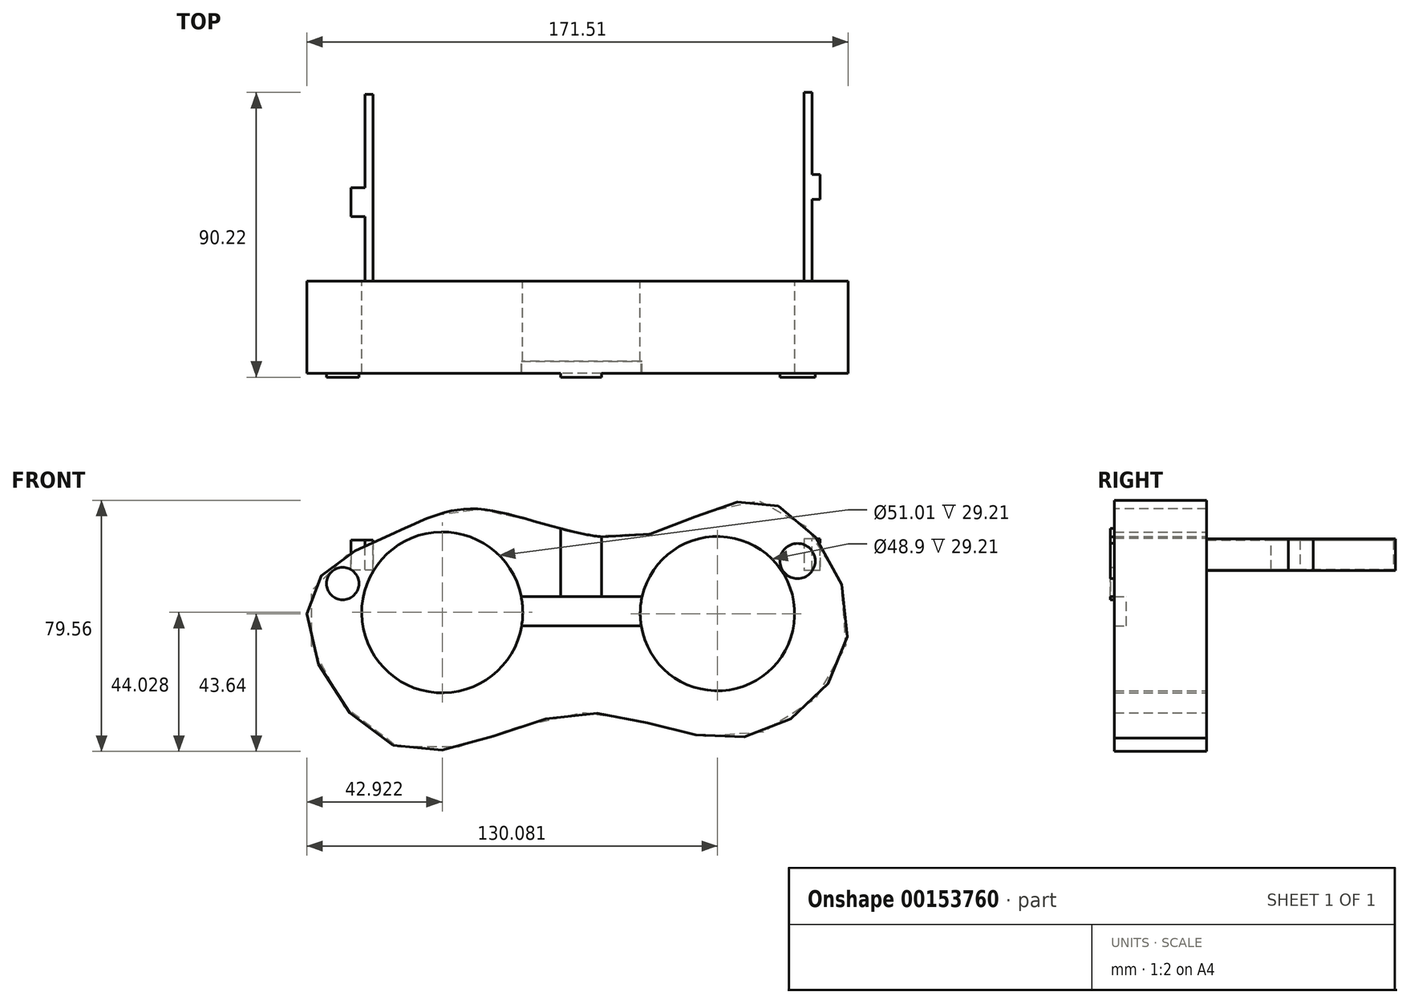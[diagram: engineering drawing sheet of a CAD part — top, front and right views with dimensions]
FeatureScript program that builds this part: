
annotation { "Feature Type Name" : "Feature", "Feature Type Description" : "" }
export const myFeature = defineFeature(function(context is Context, id is Id, definition is map)
    precondition{}
    {
        {
            var Q0;
            Q0=qCreatedBy(makeId("Front.planeOp"),FACE);
            var sketch = newSketch(context, id + "F0", { "sketchPlane" : qUnion([Q0])});
            skCircle(sketch, "E0", {"center": v(-40.35, 13.8) * mm, "radius": 25.5 * mm});
            skCircle(sketch, "E1", {"center": v(46.81, 13.42) * mm, "radius": 24.45 * mm});
            skLineSegment(sketch, "E2", {"start": v(-15.34, 18.84) * mm, "end": v(22.97, 18.84) * mm});
            skLineSegment(sketch, "E3", {"start": v(22.97, 18.84) * mm, "end": v(22.66, 9.61) * mm});
            skLineSegment(sketch, "E4", {"start": v(22.66, 9.61) * mm, "end": v(-15.19, 9.61) * mm});
            skLineSegment(sketch, "E5", {"start": v(-15.19, 9.61) * mm, "end": v(-15.34, 18.84) * mm});
            skFitSpline(sketch, "E6", {"points": [v(-55.43, 39.07) * mm, v(-28.2, 46.52) * mm, v(20.76, 37.7) * mm, v(62.09, 48.87) * mm, v(88.14, 7.74) * mm, v(54.25, -25.76) * mm, v(2.15, -18.12) * mm, v(-54.25, -28.89) * mm, v(-82.85, 17.14) * mm, v(-55.43, 39.07) * mm]});
            skSolve(sketch);
        }
        {
            var Q0;
            Q0 = qSketchRegion(id + "F0", true);
            extrude(context, id + "F1", {"entities" : qUnion([Q0]), "depth" : 29.2 * mm});
        }
        {
            var Q0;
            Q0=qCreatedBy(makeId("Right.planeOp"),FACE);
            var sketch = newSketch(context, id + "F2", { "sketchPlane" : qUnion([Q0])});
            skLineSegment(sketch, "E7", {"start": v(0, 37.12) * mm, "end": v(59.74, 37.12) * mm});
            skLineSegment(sketch, "E8", {"start": v(59.74, 37.12) * mm, "end": v(59.74, 27.13) * mm});
            skLineSegment(sketch, "E9", {"start": v(59.74, 27.13) * mm, "end": v(0, 27.13) * mm});
            skLineSegment(sketch, "E10", {"start": v(0, 37.12) * mm, "end": v(0, 27.13) * mm});
            skSolve(sketch);
        }
        {
            var Q0;
            Q0 = qSketchRegion(id + "F2", true);
            extrude(context, id + "F3", {"entities" : qUnion([Q0]), "depth" : 2.54 * mm});
        }
        {
            var Q0;
            Q0=makeQuery(id+"F3.opExtrude","SWEPT_BODY",BODY,{"disambiguationData":[OSD([sQuery(id+"F2.wireOp",EDGE,"E7"),sQuery(id+"F2.wireOp",EDGE,"E8"),sQuery(id+"F2.wireOp",EDGE,"E9"),sQuery(id+"F2.wireOp",EDGE,"E10")])]});
            var Q1;
            Q1=qCreatedBy(makeId("Right.planeOp"),FACE);
            transform(context, id + "F4", {"entities" : qUnion([Q0]), "transformType" : TransformType.TRANSLATION_DISTANCE, "transformDirection" : qUnion([Q1]), "distance" : 74.3 * mm, "makeCopy" : false});
        }
        {
            var Q0;
            Q0=qCreatedBy(makeId("Right.planeOp"),FACE);
            var sketch = newSketch(context, id + "F5", { "sketchPlane" : qUnion([Q0])});
            skLineSegment(sketch, "E11", {"start": v(0, 36.72) * mm, "end": v(59.15, 36.72) * mm});
            skLineSegment(sketch, "E12", {"start": v(59.15, 36.72) * mm, "end": v(59.15, 27.32) * mm});
            skLineSegment(sketch, "E13", {"start": v(59.15, 27.32) * mm, "end": v(0, 27.32) * mm});
            skLineSegment(sketch, "E14", {"start": v(0, 27.32) * mm, "end": v(0, 36.72) * mm});
            skSolve(sketch);
        }
        {
            var Q0;
            Q0 = qSketchRegion(id + "F5", true);
            extrude(context, id + "F6", {"entities" : qUnion([Q0]), "oppositeDirection" : true, "depth" : 2.54 * mm});
        }
        {
            var Q0;
            Q0=makeQuery(id+"F6.opExtrude","SWEPT_BODY",BODY,{"disambiguationData":[OSD([sQuery(id+"F5.wireOp",EDGE,"E11"),sQuery(id+"F5.wireOp",EDGE,"E12"),sQuery(id+"F5.wireOp",EDGE,"E13"),sQuery(id+"F5.wireOp",EDGE,"E14")])]});
            var Q1;
            Q1=makeQuery(id+"F6.opExtrude","CAP_FACE",FACE,{"disambiguationData":[OSD([sQuery(id+"F5.wireOp",EDGE,"E11"),sQuery(id+"F5.wireOp",EDGE,"E12"),sQuery(id+"F5.wireOp",EDGE,"E13"),sQuery(id+"F5.wireOp",EDGE,"E14")])],"isStart":true});
            transform(context, id + "F7", {"entities" : qUnion([Q0]), "transformType" : TransformType.TRANSLATION_DISTANCE, "transformDirection" : qUnion([Q1]), "distance" : 62.23 * mm, "oppositeDirection" : true, "makeCopy" : false});
        }
        {
            var Q0;
            {var subQ1=sQuery(id+"F0.wireOp",EDGE,"E2");Q0=makeQuery(id+"F0.imprint","IMPRINT",FACE,{"disambiguationData":[TD([[makeQuery(id+"F0.imprint","IMPRINT",EDGE,{"derivedFrom":subQ1}),-1.0]])]});}
            extrude(context, id + "F8", {"entities" : qUnion([Q0]), "operationType" : NewBodyOperationType.ADD, "depth" : 25.4 * mm});
        }
        {
            var Q0;
            Q0=makeQuery(id+"F1.opExtrude","CAP_FACE",FACE,{"disambiguationData":[OSD([sQuery(id+"F0.wireOp",EDGE,"E0"),sQuery(id+"F0.wireOp",EDGE,"E1"),sQuery(id+"F0.wireOp",EDGE,"E2"),sQuery(id+"F0.wireOp",EDGE,"E4"),sQuery(id+"F0.wireOp",EDGE,"E6")])],"isStart":false});
            var sketch = newSketch(context, id + "F9", { "sketchPlane" : qUnion([Q0])});
            skCircle(sketch, "E15", {"center": v(-71.9, 22.96) * mm, "radius": 5.14 * mm});
            skCircle(sketch, "E16", {"center": v(72.2, 30.08) * mm, "radius": 5.59 * mm});
            skSolve(sketch);
        }
        {
            var Q0;
            Q0 = qSketchRegion(id + "F9", true);
            extrude(context, id + "F10", {"entities" : qUnion([Q0]), "operationType" : NewBodyOperationType.ADD, "depth" : 1.27 * mm});
        }
        {
            var Q0;
            Q0=makeQuery(id+"F1.opExtrude","CAP_FACE",FACE,{"disambiguationData":[OSD([sQuery(id+"F0.wireOp",EDGE,"E0"),sQuery(id+"F0.wireOp",EDGE,"E1"),sQuery(id+"F0.wireOp",EDGE,"E2"),sQuery(id+"F0.wireOp",EDGE,"E4"),sQuery(id+"F0.wireOp",EDGE,"E6")])],"isStart":false});
            var sketch = newSketch(context, id + "F11", { "sketchPlane" : qUnion([Q0])});
            skLineSegment(sketch, "E17", {"start": v(-2.88, 40.37) * mm, "end": v(-2.88, 9.61) * mm});
            skLineSegment(sketch, "E18", {"start": v(-2.88, 9.61) * mm, "end": v(10.12, 9.61) * mm});
            skLineSegment(sketch, "E19", {"start": v(10.12, 9.61) * mm, "end": v(10.12, 37.75) * mm});
            skLineSegment(sketch, "E20", {"start": v(10.12, 37.75) * mm, "end": v(-2.88, 40.37) * mm});
            skSolve(sketch);
        }
        {
            var Q0;
            {var subQ1=sQuery(id+"F11.wireOp",EDGE,"E17");var subQ4=makeQuery(id+"F1.opExtrude","CAP_EDGE",EDGE,{"disambiguationData":[OSD([sQuery(id+"F0.wireOp",EDGE,"E2")])],"isStart":false});var subQ5=makeQuery(id+"F11.imprint","INTERSECT",VERTEX,{"derivedFrom":[subQ4,subQ1]});Q0=makeQuery(id+"F11.imprint","IMPRINT",FACE,{"disambiguationData":[TD([[makeQuery(id+"F11.imprint","IMPRINT",EDGE,{"disambiguationData":[TD([[subQ5,-1.0]])],"derivedFrom":subQ4}),1.0]])]});}
            extrude(context, id + "F12", {"entities" : qUnion([Q0]), "operationType" : NewBodyOperationType.ADD, "depth" : 1.27 * mm});
        }
        {
            var Q0;
            Q0=makeQuery(id+"F3.opExtrude","CAP_FACE",FACE,{"disambiguationData":[OSD([sQuery(id+"F2.wireOp",EDGE,"E7"),sQuery(id+"F2.wireOp",EDGE,"E8"),sQuery(id+"F2.wireOp",EDGE,"E9"),sQuery(id+"F2.wireOp",EDGE,"E10")])],"isStart":false});
            var sketch = newSketch(context, id + "F13", { "sketchPlane" : qUnion([Q0])});
            skLineSegment(sketch, "E21", {"start": v(25.9, 37.12) * mm, "end": v(25.9, 27.13) * mm});
            skLineSegment(sketch, "E22", {"start": v(25.9, 27.13) * mm, "end": v(33.7, 27.13) * mm});
            skLineSegment(sketch, "E23", {"start": v(33.7, 27.13) * mm, "end": v(33.7, 37.12) * mm});
            skLineSegment(sketch, "E24", {"start": v(33.7, 37.12) * mm, "end": v(25.9, 37.12) * mm});
            skSolve(sketch);
        }
        {
            var Q0;
            Q0 = qSketchRegion(id + "F13", true);
            extrude(context, id + "F14", {"entities" : qUnion([Q0]), "operationType" : NewBodyOperationType.ADD, "depth" : 2.54 * mm});
        }
        {
            var Q0;
            Q0=makeQuery(id+"F6.opExtrude","CAP_FACE",FACE,{"disambiguationData":[OSD([sQuery(id+"F5.wireOp",EDGE,"E11"),sQuery(id+"F5.wireOp",EDGE,"E12"),sQuery(id+"F5.wireOp",EDGE,"E13"),sQuery(id+"F5.wireOp",EDGE,"E14")])],"isStart":false});
            var sketch = newSketch(context, id + "F15", { "sketchPlane" : qUnion([Q0])});
            skLineSegment(sketch, "E25", {"start": v(-29.58, 36.72) * mm, "end": v(-29.58, 27.32) * mm});
            skLineSegment(sketch, "E26", {"start": v(-29.58, 27.32) * mm, "end": v(-20.37, 27.32) * mm});
            skLineSegment(sketch, "E27", {"start": v(-20.37, 27.32) * mm, "end": v(-20.37, 36.72) * mm});
            skLineSegment(sketch, "E28", {"start": v(-20.37, 36.72) * mm, "end": v(-29.58, 36.72) * mm});
            skSolve(sketch);
        }
        {
            var Q0;
            Q0 = qSketchRegion(id + "F15", true);
            extrude(context, id + "F16", {"entities" : qUnion([Q0]), "operationType" : NewBodyOperationType.ADD, "depth" : 4.44 * mm});
        }
    });
